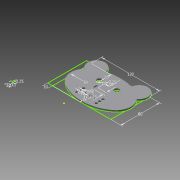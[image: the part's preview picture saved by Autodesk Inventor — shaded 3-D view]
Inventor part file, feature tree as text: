
AUTODESK INVENTOR PART (.ipt)
format: ipt  version: 2013 (Build 170138000, 138)  size: 152,064 bytes
history: native  units: mm
features: extrude x2, sketch x1
ambient origin geometry x8: Origin, YZ Plane, XZ Plane, XY Plane, X Axis, Y Axis, Z Axis, Center Point
feature tree (3):
  sketch  "Sketch1"  dims[d3=3.0mm d5=3.0mm d42=120.0mm d43=80.0mm d44=3.25mm d45=7.0mm d47=9.25mm d50=10.0mm d51=13.0mm d54=20.0mm d55=5.0mm d56=50.0mm d58=10.0mm d59=10.0mm d61=10.0mm d63=15.0mm d64=5.0mm d65=7.0mm d69=10.0mm d70=30.0mm d71=3.25mm d72=0.0mm d73=3.25mm d74=0.0mm]
  extrude  "Extrusion9"  Depth=3.0mm
  extrude  "Extrusion10"  Depth=120.0mm
